# Revit family: Interceptor_Oil-Zurn-Z1186
name_source: partatom
category: Plumbing Fixtures
units: mm (PartAtom-declared; Revit-internal decimal feet)

## family parameters
Always vertical = Yes
Cut with Voids When Loaded = No
Maintain Annotation Orientation = No
OmniClass Number = 23.45.30.00
OmniClass Title = Washing and Waste Disposal Equipment
Part Type = Normal
Room Calculation Point = No
Round Connector Dimension = Use Radius
Shared = No
Work Plane-Based = No

## types (5) — shared parameters
Assembly Code = D2090300
CW Connection = No
Default Elevation = 25 "
Description = OIL INTERCEPTOR
Extension Box Width = 4.687 "
Extented Box Length = 7 "
HW Connection = No
Main Material = Steel - Zurn - Fabricated - Acid resistant Coated
Manufacturer = Zurn Water, LLC
Manufacurer Brand = Zurn
Model = Z1186
Modified Date = 08/22/25
Product Documentation Link = https://files.zurn.com
Product Installation Sheet URL = https://files.zurn.com
Product Page URL = https://www.zurn.com
Product data url = https://www.bimobject.com
Sanitary Radius = 1 "
URL = www.zurn.com
Vent Connection = No
Vent Radius = 0.75 "
WFU = 1
Waste Connection = Yes
zero-valued in all types: CWFU, HWFU

## per-type parameters (varying)
| type | Approx. Weight (Lbs) | Dimension (H) | Dimension (K) | Dimension (M) | Height of Body (C) | Inlet/Outlet (D/E) | Inlet/Outlet Connetor Radius | Inlet/Outlet Diameter (Actual) | Inlet/Outlet Diameter (Nominal) | Overall Length (F) | Water Capacity Gal (L) | Width of Body (G) |
| Z1186-400 (2 Inch 15 G.P.M) | 77 " | 10.75 " | 11 " | 4.375 " | 14 " | 8.125 " | 1 " | 1.188 " | 1 " | 22.75 " | 9 " | 14.125 " |
| Z1186-500 (3 Inch 20 G.P.M) | 106 " | 13.25 " | 12.5 " | 5.5 " | 15.5 " | 9.375 " | 1.5 " | 1.75 " | 1.5 " | 24.625 " | 10 " | 16.75 " |
| Z1186-600 (3 Inch 25 G.P.M) | 116 " | 15.5 " | 15.25 " | 6.25 " | 18.25 " | 11.75 " | 1.5 " | 1.75 " | 1.5 " | 27.5 " | 16 " | 17.25 " |
| Z1186-700 (3 Inch 35 G.P.M) | 140 " | 15.875 " | 16.75 " | 6.375 " | 19.75 " | 12.5 " | 1.5 " | 1.75 " | 1.5 " | 29.875 " | 21 " | 19.875 " |
| Z1186-800 (3 Inch 50 G.P.M) | 140 " | 16.875 " | 21.25 " | 8.125 " | 24.25 " | 14.25 " | 1.5 " | 1.75 " | 1.5 " | 31.75 " | 30 " | 22.5 " |

## geometry (parser evidence)
native form markers: Sweep x2
no freeform markers — native parametric forms only
